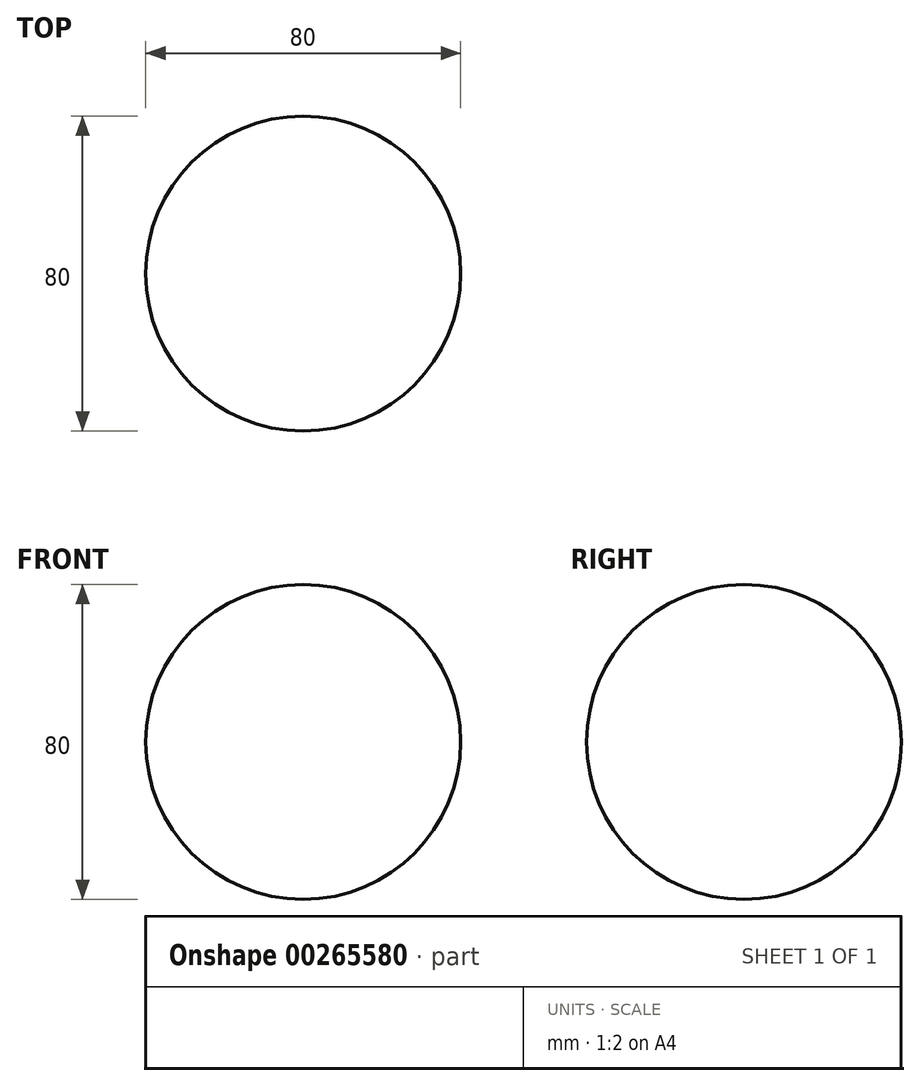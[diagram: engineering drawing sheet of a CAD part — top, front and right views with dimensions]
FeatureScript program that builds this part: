
annotation { "Feature Type Name" : "Feature", "Feature Type Description" : "" }
export const myFeature = defineFeature(function(context is Context, id is Id, definition is map)
    precondition{}
    {
        {
            var Q0;
            Q0=qCreatedBy(makeId("Front.planeOp"),FACE);
            var sketch = newSketch(context, id + "F0", { "sketchPlane" : qUnion([Q0])});
            skArc(sketch, "E0", {"start": v(0, 40) * mm, "mid": v(40, 0) * mm, "end": v(0, -40) * mm});
            skLineSegment(sketch, "E1", {"start": v(0, 40) * mm, "end": v(0, -40) * mm});
            skLineSegment(sketch, "E2", {"start": v(0, 63.61) * mm, "end": v(0, -63.88) * mm, "construction": true});
            skSolve(sketch);
        }
        {
            var Q0;
            Q0 = qSketchRegion(id + "F0", true);
            var Q1;
            Q1=sQuery(id+"F0.wireOp",EDGE,"E2");
            revolve(context, id + "F1", {"entities" : qUnion([Q0]), "axis" : qUnion([Q1]), "revolveType" : RevolveType.FULL});
        }
    });
